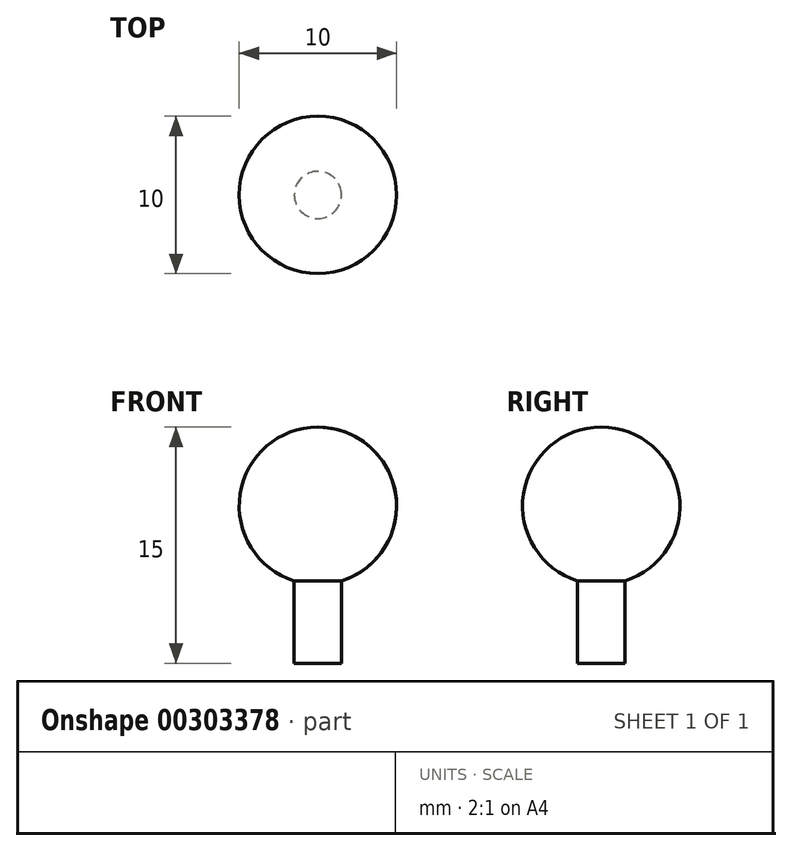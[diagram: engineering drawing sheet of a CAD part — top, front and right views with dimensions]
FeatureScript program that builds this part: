
annotation { "Feature Type Name" : "Feature", "Feature Type Description" : "" }
export const myFeature = defineFeature(function(context is Context, id is Id, definition is map)
    precondition{}
    {
        {
            var Q0;
            Q0=qCreatedBy(makeId("Front.planeOp"),FACE);
            var sketch = newSketch(context, id + "F0", { "sketchPlane" : qUnion([Q0])});
            skArc(sketch, "E0", {"start": v(1.5, -4.77) * mm, "mid": v(4.94, 0.76) * mm, "end": v(0, 5) * mm});
            skLineSegment(sketch, "E1.top", {"start": v(1.5, -10) * mm, "end": v(0, -10) * mm});
            skLineSegment(sketch, "E1.left", {"start": v(1.5, -4.77) * mm, "end": v(1.5, -10) * mm});
            skPoint(sketch, "E1.bottom.end.orphan", {"position": v(-1.5, 10) * mm});
            skPoint(sketch, "E2.orphan", {"position": v(1.5, 10) * mm});
            skLineSegment(sketch, "E3", {"start": v(0, 5) * mm, "end": v(0, -10) * mm});
            skPoint(sketch, "E4.orphan", {"position": v(-1.5, -10) * mm});
            skSolve(sketch);
        }
        {
            var Q0;
            Q0=makeQuery(id+"F0.imprint","IMPRINT",FACE,{"disambiguationData":[TD([[makeQuery(id+"F0.imprint","IMPRINT",EDGE,{"derivedFrom":sQuery(id+"F0.wireOp",EDGE,"E0")}),1.0]])]});
            var Q1;
            Q1=sQuery(id+"F0.wireOp",EDGE,"E3");
            revolve(context, id + "F1", {"entities" : qUnion([Q0]), "axis" : qUnion([Q1]), "revolveType" : RevolveType.FULL});
        }
    });
